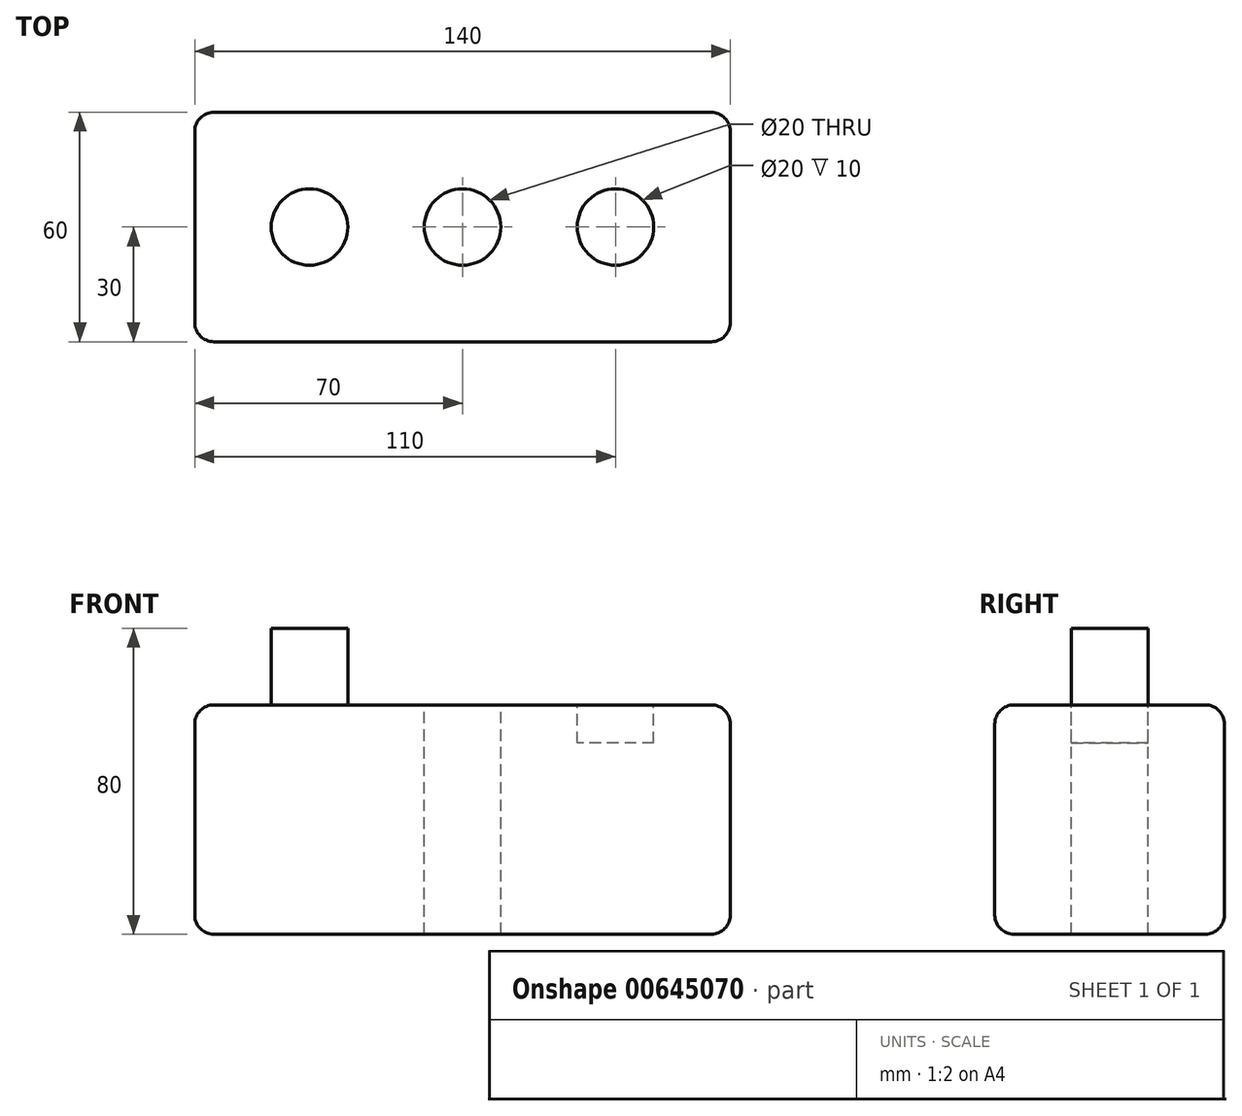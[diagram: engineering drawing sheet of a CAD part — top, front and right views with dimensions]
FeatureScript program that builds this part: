
annotation { "Feature Type Name" : "Feature", "Feature Type Description" : "" }
export const myFeature = defineFeature(function(context is Context, id is Id, definition is map)
    precondition{}
    {
        {
            var Q0;
            Q0=qCreatedBy(makeId("Top.planeOp"),FACE);
            var sketch = newSketch(context, id + "F0", { "sketchPlane" : qUnion([Q0])});
            skLineSegment(sketch, "E0.bottom", {"start": v(70, -30) * mm, "end": v(-70, -30) * mm});
            skLineSegment(sketch, "E0.top", {"start": v(70, 30) * mm, "end": v(-70, 30) * mm});
            skLineSegment(sketch, "E0.left", {"start": v(70, -30) * mm, "end": v(70, 30) * mm});
            skLineSegment(sketch, "E0.right", {"start": v(-70, -30) * mm, "end": v(-70, 30) * mm});
            skPoint(sketch, "E0.middle", {"position": v(0, 0) * mm});
            skSolve(sketch);
        }
        {
            var Q0;
            Q0 = qSketchRegion(id + "F0", true);
            extrude(context, id + "F1", {"entities" : qUnion([Q0]), "depth" : 60 * mm, "offsetDistance" : 25 * mm});
        }
        {
            var Q0;
            Q0=makeQuery(id+"F1.opExtrude","CAP_FACE",FACE,{"disambiguationData":[OSD([sQuery(id+"F0.wireOp",EDGE,"E0.bottom"),sQuery(id+"F0.wireOp",EDGE,"E0.top"),sQuery(id+"F0.wireOp",EDGE,"E0.left"),sQuery(id+"F0.wireOp",EDGE,"E0.right")])],"isStart":false});
            var sketch = newSketch(context, id + "F2", { "sketchPlane" : qUnion([Q0])});
            skCircle(sketch, "E1", {"center": v(-40, 0) * mm, "radius": 10 * mm});
            skSolve(sketch);
        }
        {
            var Q0;
            Q0=makeQuery(id+"F2.imprint","IMPRINT",FACE,{"disambiguationData":[TD([[makeQuery(id+"F2.imprint","IMPRINT",EDGE,{"derivedFrom":sQuery(id+"F2.wireOp",EDGE,"E1")}),-1.0]])]});
            var sketch = newSketch(context, id + "F3", { "sketchPlane" : qUnion([Q0])});
            skCircle(sketch, "E2", {"center": v(40, 0) * mm, "radius": 10 * mm});
            skSolve(sketch);
        }
        {
            var Q0;
            Q0=makeQuery(id+"F2.imprint","IMPRINT",FACE,{"disambiguationData":[TD([[makeQuery(id+"F2.imprint","IMPRINT",EDGE,{"derivedFrom":sQuery(id+"F2.wireOp",EDGE,"E1")}),-1.0]])]});
            var sketch = newSketch(context, id + "F4", { "sketchPlane" : qUnion([Q0])});
            skCircle(sketch, "E3", {"center": v(0, 0) * mm, "radius": 10 * mm});
            skSolve(sketch);
        }
        {
            var Q0;
            Q0 = qSketchRegion(id + "F2", true);
            extrude(context, id + "F5", {"entities" : qUnion([Q0]), "operationType" : NewBodyOperationType.ADD, "depth" : 20 * mm, "offsetDistance" : 25 * mm});
        }
        {
            var Q0;
            Q0 = qSketchRegion(id + "F4", true);
            extrude(context, id + "F6", {"entities" : qUnion([Q0]), "operationType" : NewBodyOperationType.REMOVE, "oppositeDirection" : true, "depth" : 71.6 * mm, "offsetDistance" : 25 * mm});
        }
        {
            var Q0;
            Q0 = qSketchRegion(id + "F3", true);
            extrude(context, id + "F7", {"entities" : qUnion([Q0]), "operationType" : NewBodyOperationType.REMOVE, "oppositeDirection" : true, "depth" : 10 * mm, "offsetDistance" : 25 * mm});
        }
        {
            var Q0;
            Q0=makeQuery(id+"F1.opExtrude","CAP_EDGE",EDGE,{"disambiguationData":[OSD([sQuery(id+"F0.wireOp",EDGE,"E0.top")])],"isStart":false});
            var Q1;
            Q1=makeQuery(id+"F1.opExtrude","CAP_EDGE",EDGE,{"disambiguationData":[OSD([sQuery(id+"F0.wireOp",EDGE,"E0.right")])],"isStart":false});
            var Q2;
            Q2=makeQuery(id+"F1.opExtrude","CAP_EDGE",EDGE,{"disambiguationData":[OSD([sQuery(id+"F0.wireOp",EDGE,"E0.bottom")])],"isStart":false});
            var Q3;
            Q3=makeQuery(id+"F1.opExtrude","CAP_EDGE",EDGE,{"disambiguationData":[OSD([sQuery(id+"F0.wireOp",EDGE,"E0.left")])],"isStart":false});
            fillet(context, id + "F8", {"entities" : qUnion([Q0, Q1, Q2, Q3]), "radius" : 5 * mm, "tangentPropagation" : true, "allowEdgeOverflow" : false});
        }
        {
            var Q0;
            Q0=makeQuery(id+"F1.opExtrude","CAP_EDGE",EDGE,{"disambiguationData":[OSD([sQuery(id+"F0.wireOp",EDGE,"E0.bottom")])],"isStart":true});
            var Q1;
            Q1=makeQuery(id+"F1.opExtrude","SWEPT_EDGE",EDGE,{"disambiguationData":[OSD([sQuery(id+"F0.wireOp",EDGE,"E0.bottom"),sQuery(id+"F0.wireOp",EDGE,"E0.left")])]});
            fillet(context, id + "F9", {"entities" : qUnion([Q0, Q1]), "radius" : 5 * mm, "tangentPropagation" : true, "allowEdgeOverflow" : false});
        }
        {
            var Q0;
            Q0=makeQuery(id+"F1.opExtrude","SWEPT_EDGE",EDGE,{"disambiguationData":[OSD([sQuery(id+"F0.wireOp",EDGE,"E0.bottom"),sQuery(id+"F0.wireOp",EDGE,"E0.right")])]});
            fillet(context, id + "F10", {"entities" : qUnion([Q0]), "radius" : 5 * mm, "tangentPropagation" : true, "allowEdgeOverflow" : false});
        }
        {
            var Q0;
            Q0=makeQuery(id+"F1.opExtrude","CAP_EDGE",EDGE,{"disambiguationData":[OSD([sQuery(id+"F0.wireOp",EDGE,"E0.top")])],"isStart":true});
            fillet(context, id + "F11", {"entities" : qUnion([Q0]), "radius" : 5 * mm, "tangentPropagation" : true, "allowEdgeOverflow" : false});
        }
        {
            var Q0;
            Q0=makeQuery(id+"F1.opExtrude","SWEPT_EDGE",EDGE,{"disambiguationData":[OSD([sQuery(id+"F0.wireOp",EDGE,"E0.top"),sQuery(id+"F0.wireOp",EDGE,"E0.left")])]});
            fillet(context, id + "F12", {"entities" : qUnion([Q0]), "radius" : 5 * mm, "tangentPropagation" : true, "allowEdgeOverflow" : false});
        }
    });
